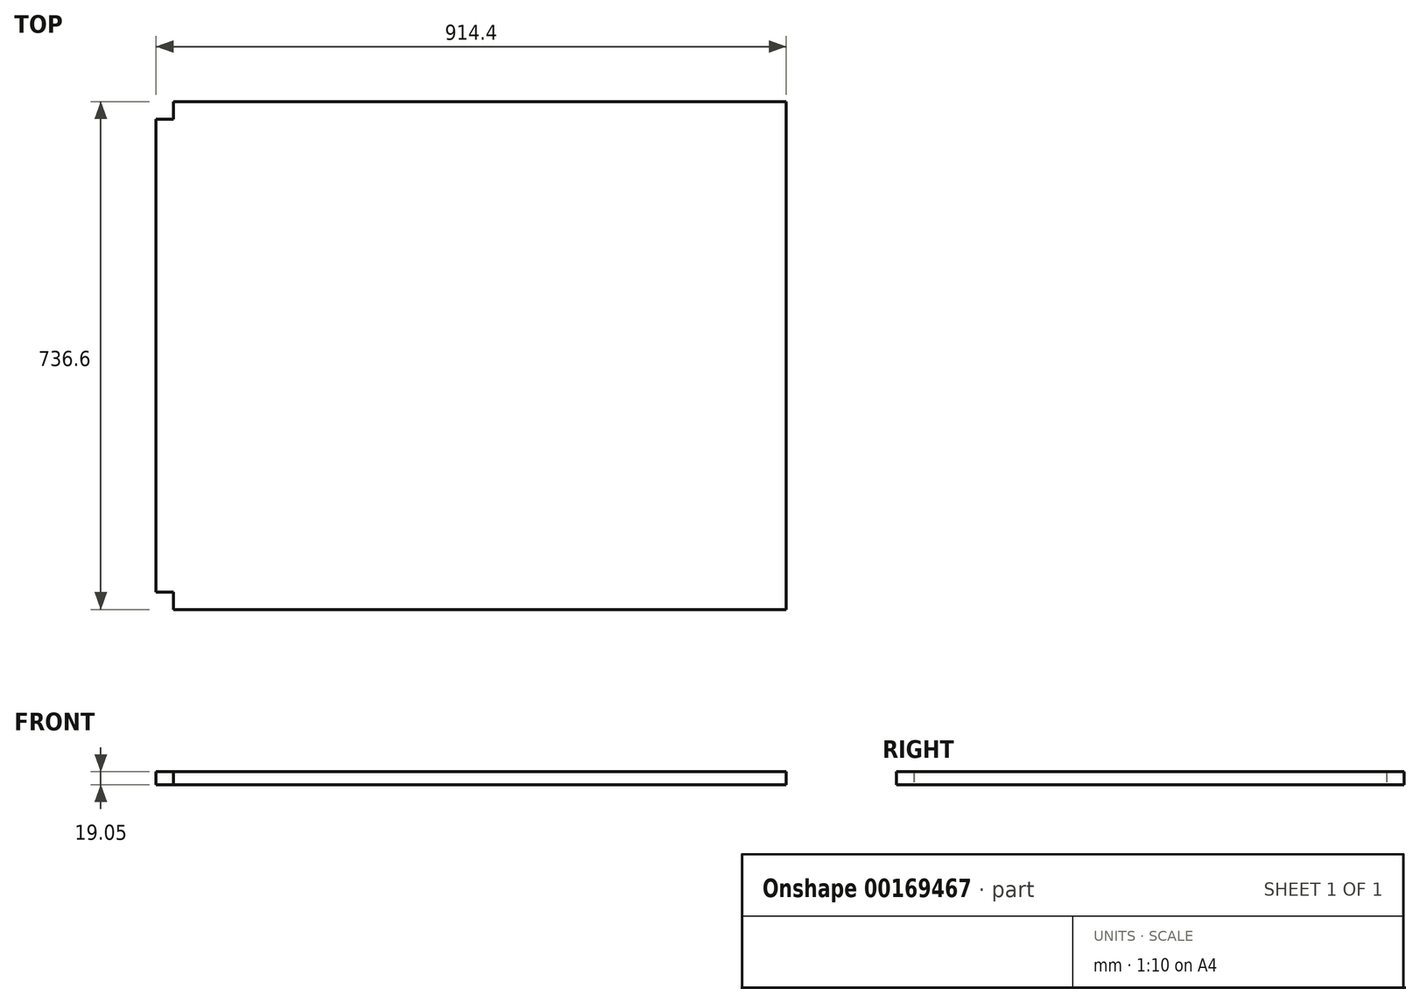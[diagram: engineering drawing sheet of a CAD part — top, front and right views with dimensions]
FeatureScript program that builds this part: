
annotation { "Feature Type Name" : "Feature", "Feature Type Description" : "" }
export const myFeature = defineFeature(function(context is Context, id is Id, definition is map)
    precondition{}
    {
        {
            var Q0;
            Q0=qCreatedBy(makeId("Top.planeOp"),FACE);
            var sketch = newSketch(context, id + "F0", { "sketchPlane" : qUnion([Q0])});
            skLineSegment(sketch, "E0.bottom", {"start": v(-218.28, 158.89) * mm, "end": v(670.72, 158.89) * mm});
            skLineSegment(sketch, "E0.left", {"start": v(-243.68, 133.49) * mm, "end": v(-243.68, -552.31) * mm});
            skLineSegment(sketch, "E0.right", {"start": v(670.72, 158.89) * mm, "end": v(670.72, -577.71) * mm});
            skLineSegment(sketch, "E1", {"start": v(-218.28, -577.71) * mm, "end": v(-218.28, -552.31) * mm});
            skLineSegment(sketch, "E2", {"start": v(-218.28, -552.31) * mm, "end": v(-243.68, -552.31) * mm});
            skLineSegment(sketch, "E3", {"start": v(-218.28, 158.89) * mm, "end": v(-218.28, 133.49) * mm});
            skLineSegment(sketch, "E4", {"start": v(-218.28, 133.49) * mm, "end": v(-243.68, 133.49) * mm});
            skLineSegment(sketch, "E5", {"start": v(-218.28, -577.71) * mm, "end": v(670.72, -577.71) * mm});
            skSolve(sketch);
        }
        {
            var Q0;
            Q0=qSketchRegion(id+"F0",true);
            extrude(context, id + "F1", {"entities" : qUnion([Q0]), "depth" : 19.05 * mm});
        }
    });
